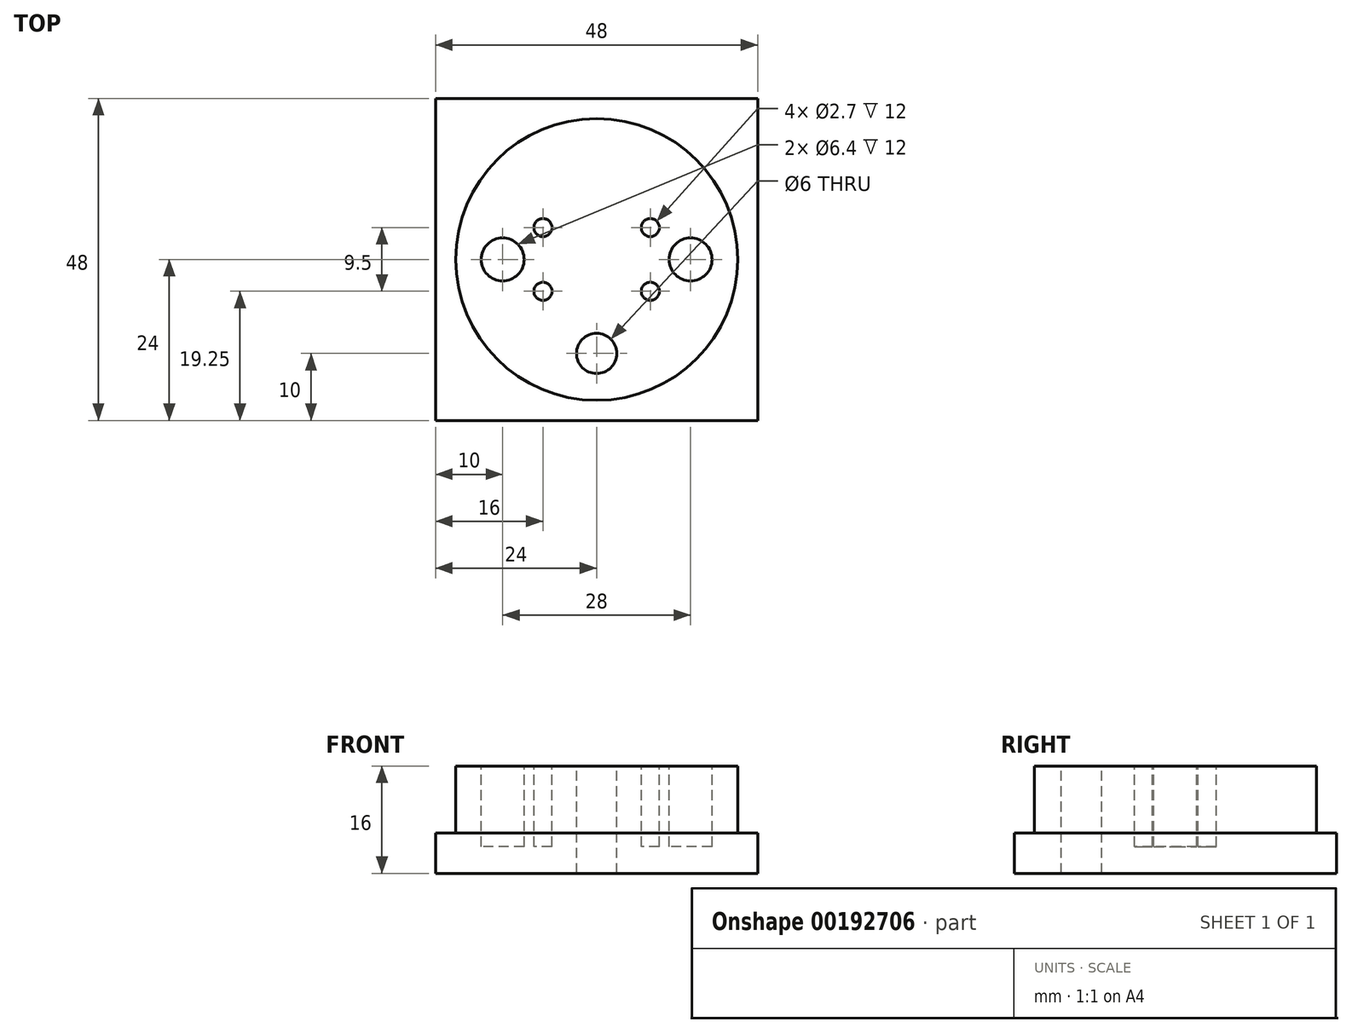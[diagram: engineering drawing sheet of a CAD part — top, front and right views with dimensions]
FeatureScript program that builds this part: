
annotation { "Feature Type Name" : "Feature", "Feature Type Description" : "" }
export const myFeature = defineFeature(function(context is Context, id is Id, definition is map)
    precondition{}
    {
        {
            var Q0;
            Q0=qCreatedBy(makeId("Top.planeOp"),FACE);
            var sketch = newSketch(context, id + "F0", { "sketchPlane" : qUnion([Q0])});
            skCircle(sketch, "E0", {"center": v(0, 0) * mm, "radius": 21 * mm, "construction": true});
            skLineSegment(sketch, "E1.bottom", {"start": v(-24, 24) * mm, "end": v(24, 24) * mm});
            skLineSegment(sketch, "E1.top", {"start": v(-24, -24) * mm, "end": v(24, -24) * mm});
            skLineSegment(sketch, "E1.left", {"start": v(-24, 24) * mm, "end": v(-24, -24) * mm});
            skLineSegment(sketch, "E1.right", {"start": v(24, 24) * mm, "end": v(24, -24) * mm});
            skSolve(sketch);
        }
        {
            var Q0;
            Q0 = qSketchRegion(id + "F0", true);
            extrude(context, id + "F1", {"entities" : qUnion([Q0]), "depth" : 6 * mm});
        }
        {
            var Q0;
            Q0=makeQuery(id+"F1.opExtrude","CAP_FACE",FACE,{"disambiguationData":[OSD([sQuery(id+"F0.wireOp",EDGE,"E1.bottom"),sQuery(id+"F0.wireOp",EDGE,"E1.top"),sQuery(id+"F0.wireOp",EDGE,"E1.left"),sQuery(id+"F0.wireOp",EDGE,"E1.right")])],"isStart":false});
            var sketch = newSketch(context, id + "F2", { "sketchPlane" : qUnion([Q0])});
            skCircle(sketch, "E2", {"center": v(0, 0) * mm, "radius": 21 * mm});
            skSolve(sketch);
        }
        {
            var Q0;
            Q0 = qSketchRegion(id + "F2", true);
            extrude(context, id + "F3", {"entities" : qUnion([Q0]), "operationType" : NewBodyOperationType.ADD, "depth" : 10 * mm});
        }
        {
            var Q0;
            Q0=makeQuery(id+"F3.opExtrude","CAP_FACE",FACE,{"disambiguationData":[OSD([sQuery(id+"F2.wireOp",EDGE,"E2")])],"isStart":false});
            var sketch = newSketch(context, id + "F4", { "sketchPlane" : qUnion([Q0])});
            skCircle(sketch, "E3", {"center": v(-14, 0) * mm, "radius": 3.2 * mm});
            skCircle(sketch, "E4", {"center": v(14, 0) * mm, "radius": 3.2 * mm});
            skLineSegment(sketch, "E5.bottom", {"start": v(-8, 4.75) * mm, "end": v(8, 4.75) * mm, "construction": true});
            skLineSegment(sketch, "E5.top", {"start": v(-8, -4.75) * mm, "end": v(8, -4.75) * mm, "construction": true});
            skLineSegment(sketch, "E5.left", {"start": v(-8, 4.75) * mm, "end": v(-8, -4.75) * mm, "construction": true});
            skLineSegment(sketch, "E5.right", {"start": v(8, 4.75) * mm, "end": v(8, -4.75) * mm, "construction": true});
            skCircle(sketch, "E6", {"center": v(-8, 4.75) * mm, "radius": 1.35 * mm});
            skCircle(sketch, "E7", {"center": v(8, 4.75) * mm, "radius": 1.35 * mm});
            skCircle(sketch, "E8", {"center": v(-8, -4.75) * mm, "radius": 1.35 * mm});
            skCircle(sketch, "E9", {"center": v(8, -4.75) * mm, "radius": 1.35 * mm});
            skSolve(sketch);
        }
        {
            var Q0;
            Q0 = qSketchRegion(id + "F4", true);
            extrude(context, id + "F5", {"entities" : qUnion([Q0]), "operationType" : NewBodyOperationType.REMOVE, "oppositeDirection" : true, "depth" : 12 * mm});
        }
        {
            var Q0;
            Q0=makeQuery(id+"F3.opExtrude","CAP_FACE",FACE,{"disambiguationData":[OSD([sQuery(id+"F2.wireOp",EDGE,"E2")])],"isStart":false});
            var sketch = newSketch(context, id + "F6", { "sketchPlane" : qUnion([Q0])});
            skCircle(sketch, "E10", {"center": v(0, -14) * mm, "radius": 3 * mm});
            skSolve(sketch);
        }
        {
            var Q0;
            Q0 = qSketchRegion(id + "F6", true);
            extrude(context, id + "F7", {"entities" : qUnion([Q0]), "operationType" : NewBodyOperationType.REMOVE, "endBound" : BoundingType.THROUGH_ALL, "oppositeDirection" : true, "depth" : 25 * mm});
        }
    });
